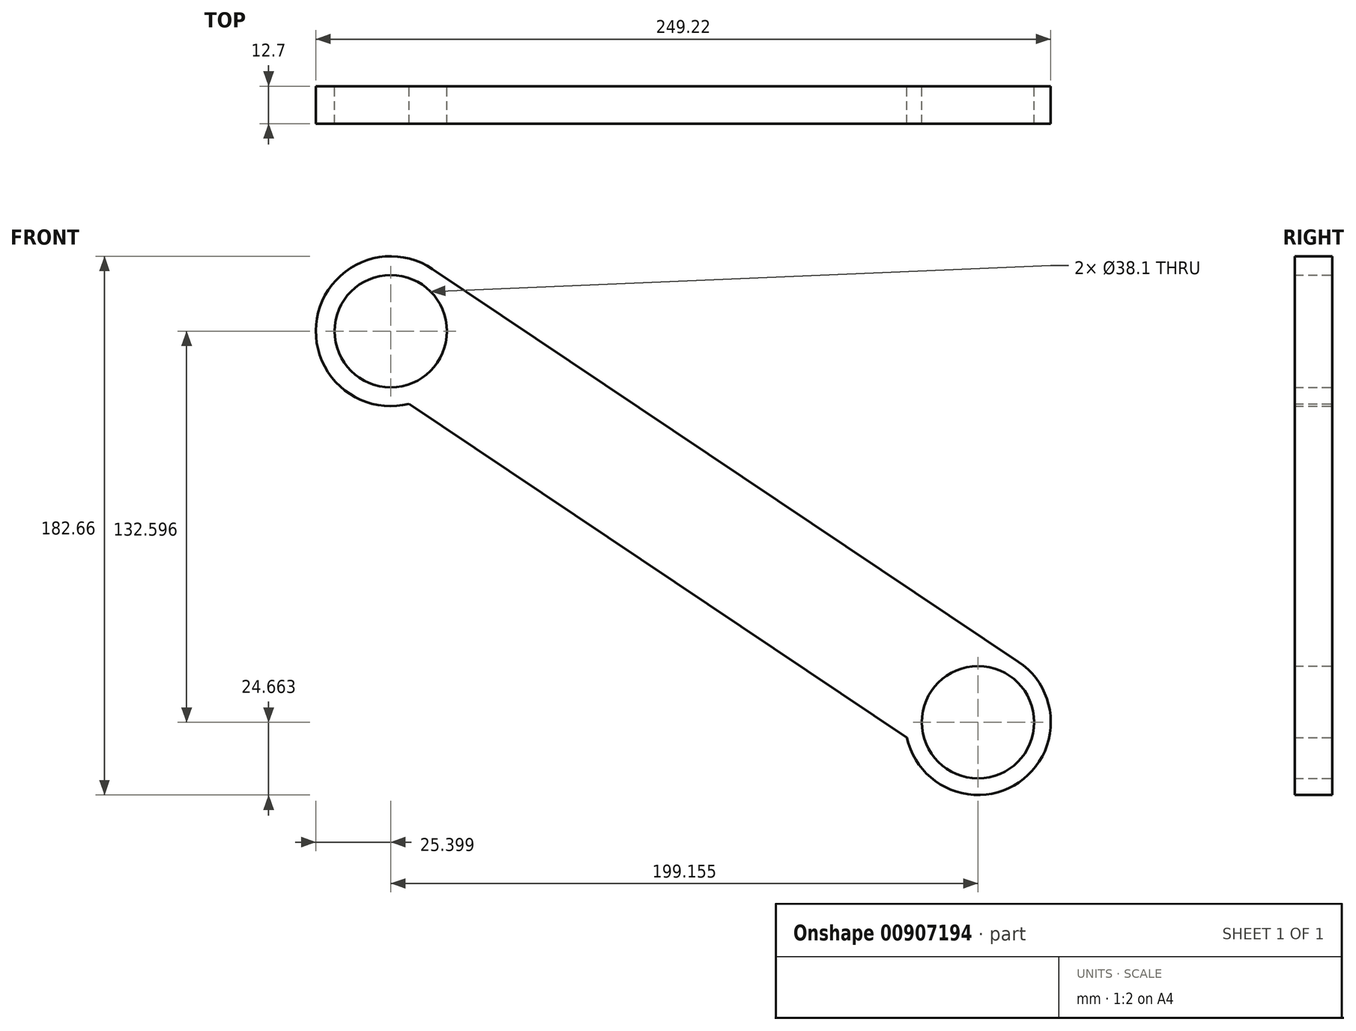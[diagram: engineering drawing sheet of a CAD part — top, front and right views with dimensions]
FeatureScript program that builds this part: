
annotation { "Feature Type Name" : "Feature", "Feature Type Description" : "" }
export const myFeature = defineFeature(function(context is Context, id is Id, definition is map)
    precondition{}
    {
        {
            var Q0;
            Q0=qCreatedBy(makeId("Front.planeOp"),FACE);
            var sketch = newSketch(context, id + "F0", { "sketchPlane" : qUnion([Q0])});
            skLineSegment(sketch, "E0", {"start": v(-92.49, 87.74) * mm, "end": v(106.26, -45.47) * mm});
            skLineSegment(sketch, "E1", {"start": v(-100.39, 42.02) * mm, "end": v(68.4, -71.11) * mm});
            skArc(sketch, "E2", {"start": v(-92.49, 87.74) * mm, "mid": v(-131.66, 70.96) * mm, "end": v(-100.39, 42.02) * mm});
            skArc(sketch, "E3", {"start": v(106.26, -45.47) * mm, "mid": v(106.36, -86.38) * mm, "end": v(68.4, -71.11) * mm});
            skCircle(sketch, "E4", {"center": v(-106.63, 66.64) * mm, "radius": 19.05 * mm});
            skCircle(sketch, "E5", {"center": v(92.52, -65.96) * mm, "radius": 19.05 * mm});
            skSolve(sketch);
        }
        {
            var Q0;
            Q0 = qSketchRegion(id + "F0", true);
            extrude(context, id + "F1", {"entities" : qUnion([Q0]), "endBound" : BoundingType.SYMMETRIC, "depth" : 12.7 * mm, "offsetDistance" : 25.4 * mm});
        }
    });
